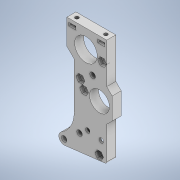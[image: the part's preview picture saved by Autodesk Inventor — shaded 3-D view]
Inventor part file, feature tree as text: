
AUTODESK INVENTOR PART (.ipt)
format: ipt  version: 2020 (Build 240168000, 168)  size: 551,424 bytes
history: native  units: mm
features: extrude x14, sketch x10, fillet x5, projected_geometry x5, thread x2, chamfer x1, mirror x1
ambient origin geometry x8: Origin, YZ Plane, XZ Plane, XY Plane, X Axis, Y Axis, Z Axis, Center Point
bodies: Solid1 (feature_tree)
feature tree (38):
  extrude  "Extrusion1"  Depth=23.5mm
  fillet  "Fillet1"  Radius=23.5mm
  fillet  "Fillet2"  Radius=6.0mm
  extrude  "Extrusion2"  Depth=3.0mm
  extrude  "Extrusion3"  Depth=4.0mm
  thread  "Thread1"  [1 undecoded]
  thread  "Thread2"  [1 undecoded]
  extrude  "Extrusion4"  Depth=24.75mm
  extrude  "Extrusion5"  Depth=2.1mm
  extrude  "Extrusion6"  Depth=4.0mm
  extrude  "Extrusion7"  TaperAngle=45.0deg  [1 undecoded]
  extrude  "Extrusion8"  Depth=12.0mm
  extrude  "Extrusion9"  TaperAngle=135.0deg  [1 undecoded]
  extrude  "Extrusion10"  Depth=5.0mm TaperAngle=0.0deg
  fillet  "Fillet3"  Radius=3.0mm
  extrude  "Extrusion11"  Depth=10.0mm
  chamfer  "Chamfer1"  Distance=3.0mm
  fillet  "Fillet4"  Radius=2.5mm
  extrude  "Extrusion12"  Depth=0.5mm
  extrude  "Extrusion13"  Depth=7.5mm
  extrude  "Extrusion14"  Depth=0.5mm
  fillet  "Fillet5"  Radius=15.0mm
  mirror  "Mirror2"
  sketch  "Sketch3"  dims[d0=3.0mm d1=6.0mm d2=23.5mm d3=6.0mm]
  projected_geometry  "Projected Loop1"
  sketch  "Sketch5"  dims[d4=0.0mm d5=3.0mm]
  sketch  "Sketch7"  dims[d6=18.0mm d7=56.0mm d8=11.0mm d9=4.0mm]
  sketch  "Sketch8"  dims[d10=24.75mm d11=12.5mm]
  projected_geometry  "Projected Loop2"
  sketch  "Sketch10"  dims[d12=22.3mm d14=2.1mm]
  sketch  "Sketch13"  dims[d18=30.0mm d20=360.0deg d22=4.0mm]
  sketch  "Sketch15"  dims[d23=14.0mm d24=45.0deg]
  sketch  "Sketch17"  dims[d25=3.0mm d26=12.0mm]
  projected_geometry  "Projected Loop3"
  sketch  "Sketch21"  dims[d27=6.0mm d28=135.0deg]
  projected_geometry  "Projected Loop5"
  sketch  "Sketch22"  dims[d29=135.0deg d30=5.0mm d31=0.0mm d32=3.0mm d33=10.0mm d34=3.0mm d35=2.5mm d36=13.5mm d37=7.5mm d38=2.5mm d39=15.0mm d40=12.5mm d41=1.0mm d42=15.0mm d43=12.75mm d44=20.0mm d45=23.75mm d46=3.0mm d47=0.0mm d48=2.0mm d49=2.0mm d50=2.5mm d51=2.5mm d52=3.0mm d53=3.0mm d54=4.5mm d55=0.0mm d56=7.0mm d57=0.0mm d58=7.0mm d59=0.0mm d60=8.5mm d61=270.0deg d62=4.0mm d63=4.0mm d64=4.0mm d65=3.0mm d66=0.0mm d67=5.5mm d68=2.0mm d69=0.0mm d70=4.0mm d71=1.85mm d72=4.0mm d73=1.85mm d74=1.0mm d75=2.8mm d76=2.8mm d77=1.0mm d78=10.0mm d79=0.0mm d82=3.1mm d83=11.15mm d84=2.1mm d85=2.1mm d86=2.1mm d87=5.5mm d88=3.5mm d89=25.75mm d90=30.25mm d91=2.5mm d92=11.75mm d93=24.0mm d94=8.0mm d95=2.1mm d96=2.1mm d98=2.1mm d99=1.8mm d100=0.0mm d101=2.1mm d102=2.1mm d103=2.1mm d104=1.8mm d105=0.0mm d117=3.9mm d118=0.0mm d119=18.0mm d120=6.5mm d121=0.0mm d122=1.0mm d125=5.0mm d126=7.25mm d127=2.5mm d128=5.0mm d129=15.0mm d130=5.0mm d131=5.0mm d132=90.0deg d133=135.0deg d135=135.0deg d136=135.0deg d137=3.0mm d138=0.0mm d139=0.9mm d140=2.0mm d141=45.0deg d142=4.0mm d143=2.0mm d144=2.6mm d145=3.625mm d146=10.0mm d147=0.0mm d148=2.05mm d149=2.4mm d150=0.0mm d151=4.5mm d154=1.0mm d155=0.0mm d156=2.0mm d157=2.8mm d80=0.5mm d81=0.872665mm d106=0.872665mm d123=0.872665mm d134=0.5mm d153=0.5mm d158=0.5mm d159=0.872665mm d160=0.5mm d161=0.872665mm]
  projected_geometry  "Projected Loop6"
note: 4 required parameter values undecoded (feature->parameter linkage not recoverable at this tier; creation-order binding heuristic only, values carry confidence <= 0.55)
